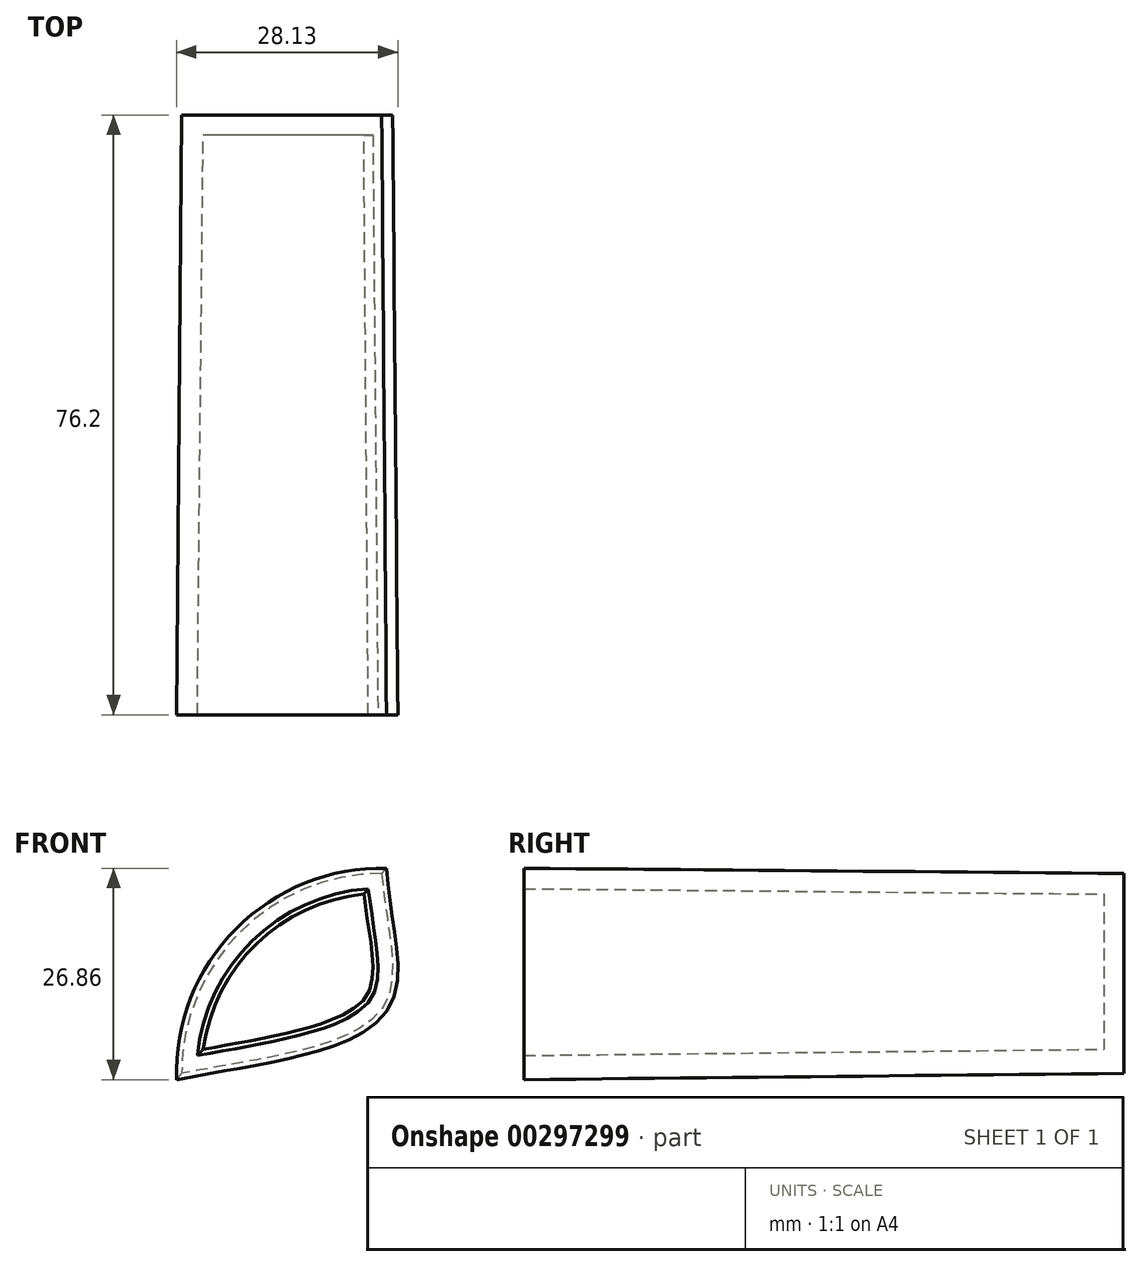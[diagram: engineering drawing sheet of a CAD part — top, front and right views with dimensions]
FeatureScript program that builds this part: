
annotation { "Feature Type Name" : "Feature", "Feature Type Description" : "" }
export const myFeature = defineFeature(function(context is Context, id is Id, definition is map)
    precondition{}
    {
        {
            var Q0;
            Q0=qCreatedBy(makeId("Front.planeOp"),FACE);
            var sketch = newSketch(context, id + "F0", { "sketchPlane" : qUnion([Q0])});
            skPoint(sketch, "E0.visualSharp", {"position": v(-64.7, 72.92) * mm});
            skArc(sketch, "E0.filletArc", {"start": v(-39.3, 72.92) * mm, "mid": v(-57.26, 65.48) * mm, "end": v(-64.7, 47.52) * mm});
            skPoint(sketch, "E1.visualSharp", {"position": v(87.7, 72.92) * mm});
            skArc(sketch, "E1.filletArc", {"start": v(87.7, 47.52) * mm, "mid": v(80.27, 65.48) * mm, "end": v(62.3, 72.92) * mm});
            skPoint(sketch, "E2.visualSharp", {"position": v(-64.7, -28.68) * mm});
            skArc(sketch, "E2.filletArc", {"start": v(-64.7, -3.28) * mm, "mid": v(-57.26, -21.24) * mm, "end": v(-39.3, -28.68) * mm});
            skPoint(sketch, "E3.visualSharp", {"position": v(87.7, -28.68) * mm});
            skFitSpline(sketch, "E4", {"points": [v(-39.3, 72.92) * mm, v(-39.3, 55.66) * mm, v(-64.7, 47.52) * mm, v(-92.4, 36.4) * mm, v(-119.92, 4.06) * mm, v(-135.75, -26.9) * mm, v(-105.13, -31.03) * mm, v(-91.03, 0) * mm, v(-77.26, 0) * mm, v(-64.7, -3.28) * mm, v(-39.3, -28.68) * mm, v(-31.51, -47.54) * mm, v(0, -58.2) * mm, v(16.65, -48.57) * mm, v(36.26, -18.99) * mm, v(62.3, -28.68) * mm, v(79.26, -38.94) * mm, v(97.15, -35.5) * mm, v(99.9, -13.83) * mm, v(103.34, 23.67) * mm, v(87.7, 47.52) * mm, v(68.94, 51.88) * mm, v(62.3, 72.92) * mm, v(51.74, 85.94) * mm, v(14.24, 92.47) * mm, v(5.3, 83.18) * mm, v(-13.28, 81.12) * mm, v(-34.6, 88.34) * mm, v(-39.3, 72.92) * mm]});
            skSolve(sketch);
        }
        {
            var Q0;
            Q0=makeQuery(id+"F0.imprint","IMPRINT",FACE,{"disambiguationData":[TD([[makeQuery(id+"F0.imprint","IMPRINT",EDGE,{"derivedFrom":sQuery(id+"F0.wireOp",EDGE,"E0.filletArc")}),1.0]])]});
            extrude(context, id + "F1", {"entities" : qUnion([Q0]), "depth" : 76.2 * mm, "hasDraft" : true, "draftAngle" : 0.5 * degree});
        }
        {
            var Q0;
            Q0=makeQuery(id+"F1.opExtrude","CAP_FACE",FACE,{"disambiguationData":[OSD([sQuery(id+"F0.wireOp",EDGE,"E0.filletArc"),sQuery(id+"F0.wireOp",EDGE,"E1.filletArc"),sQuery(id+"F0.wireOp",EDGE,"E2.filletArc"),sQuery(id+"F0.wireOp",EDGE,"E4"),sQuery(id+"F0.wireOp",EDGE,"E4"),sQuery(id+"F0.wireOp",EDGE,"E4")])],"isStart":false});
            shell(context, id + "F2", {"entities" : qUnion([Q0]), "thickness" : 2.54 * mm});
        }
    });
